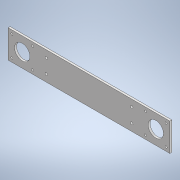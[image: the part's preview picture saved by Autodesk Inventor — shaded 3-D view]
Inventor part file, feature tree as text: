
AUTODESK INVENTOR PART (.ipt)
format: ipt  version: 2021 (Build 250183000, 183)  size: 130,048 bytes
history: native  units: mm
features: other x9, sketch x3, hole x3, extrude x1, mirror x1
ambient origin geometry x8: Origin, YZ Plane, XZ Plane, XY Plane, X Axis, Y Axis, Z Axis, Center Point
bodies: Body1 (feature_tree)
feature tree (17):
  other  "Sólido1"
  extrude  "Extrusão1"  Depth=42.0mm
  sketch  "Esboço2"  dims[d2=3.0mm d3=0.0mm d4=42.0mm]
  hole  "Furo1"  [1 undecoded]
  hole  "Furo2"  [1 undecoded]
  mirror  "Espelhamento1"
  hole  "Furo3"  [1 undecoded]
  sketch  "Esboço1"  dims[d0=242.0mm d1=42.0mm]
  sketch  "Esboço3"  dims[d5=42.0mm d6=31.0mm d7=31.0mm d8=3.0mm d9=6.0mm d10=4.0mm d11=2.0mm d12=90.0deg d13=8.0mm d14=20.594885mm d15=23.0mm d16=6.0mm d17=4.0mm d18=2.0mm d19=90.0deg d20=8.0mm d21=20.594885mm d22=4.0mm d23=8.0mm d24=4.0mm d25=2.0mm d26=90.0deg d27=8.0mm d28=20.594885mm]
  other  "Referência1"
  other  "Referência2"
  other  "Referência3"
  other  "Referência4"
  parser-record x1  (decoder bookkeeping rows leaked as tree rows — omitted from the tree; the rows remain in map.json)
  other  "Omni Robot.iam"
  other  "chapa lentral:2"
  other  "chapa lentral:1"
note: 3 required parameter values undecoded (feature->parameter linkage not recoverable at this tier; creation-order binding heuristic only, values carry confidence <= 0.55)
note: 1 file-system path scrubbed to <path> (originals preserved in map.json)
